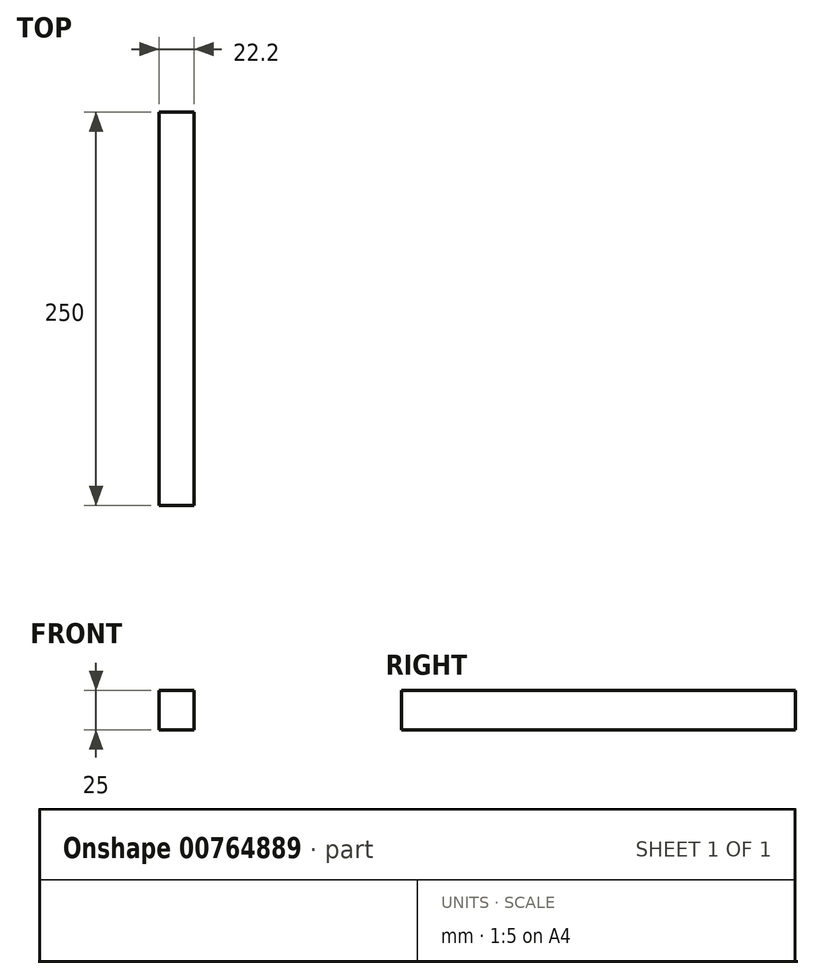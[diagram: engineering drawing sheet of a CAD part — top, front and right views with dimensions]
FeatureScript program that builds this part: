
annotation { "Feature Type Name" : "Feature", "Feature Type Description" : "" }
export const myFeature = defineFeature(function(context is Context, id is Id, definition is map)
    precondition{}
    {
        {
            var Q0;
            Q0=qCreatedBy(makeId("Front.planeOp"),FACE);
            var sketch = newSketch(context, id + "F0", { "sketchPlane" : qUnion([Q0])});
            skLineSegment(sketch, "E0.bottom", {"start": v(11.1, -12.5) * mm, "end": v(-11.1, -12.5) * mm});
            skLineSegment(sketch, "E0.top", {"start": v(11.1, 12.5) * mm, "end": v(-11.1, 12.5) * mm});
            skLineSegment(sketch, "E0.left", {"start": v(11.1, -12.5) * mm, "end": v(11.1, 12.5) * mm});
            skLineSegment(sketch, "E0.right", {"start": v(-11.1, -12.5) * mm, "end": v(-11.1, 12.5) * mm});
            skPoint(sketch, "E0.middle", {"position": v(0, 0) * mm});
            skSolve(sketch);
        }
        {
            var Q0;
            Q0 = qSketchRegion(id + "F0", true);
            extrude(context, id + "F1", {"entities" : qUnion([Q0]), "oppositeDirection" : true, "depth" : 250 * mm, "offsetDistance" : 25 * mm});
        }
    });
